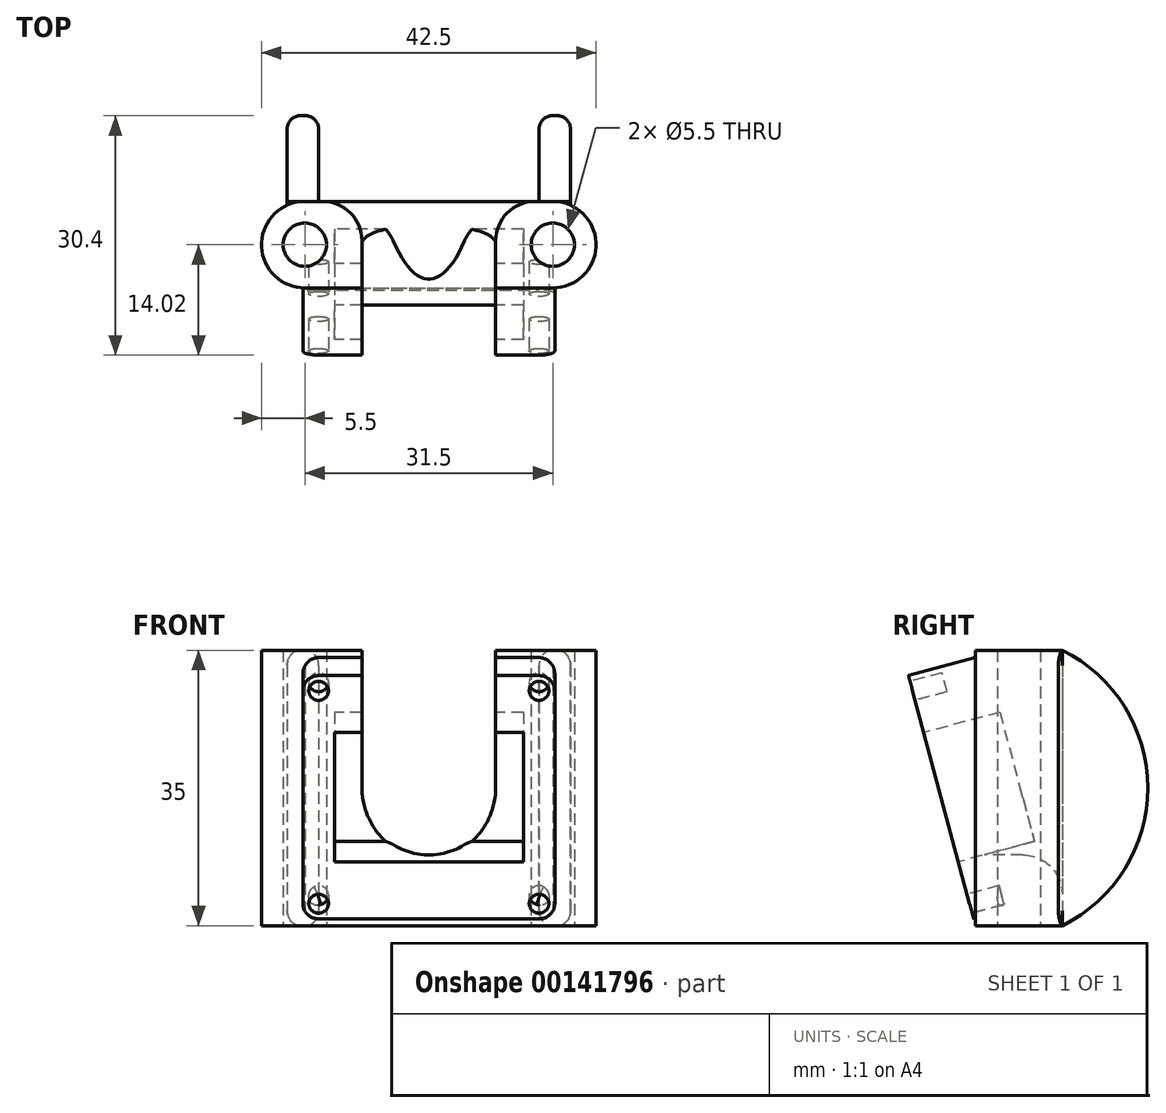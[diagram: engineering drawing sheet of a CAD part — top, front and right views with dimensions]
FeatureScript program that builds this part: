
annotation { "Feature Type Name" : "Feature", "Feature Type Description" : "" }
export const myFeature = defineFeature(function(context is Context, id is Id, definition is map)
    precondition{}
    {
        {
            var Q0;
            Q0=qCreatedBy(makeId("Top.planeOp"),FACE);
            var sketch = newSketch(context, id + "F0", { "sketchPlane" : qUnion([Q0])});
            skLineSegment(sketch, "E0", {"start": v(-18.5, 0) * mm, "end": v(18.5, 0) * mm, "construction": true});
            skCircle(sketch, "E1", {"center": v(-15.75, 0) * mm, "radius": 2.75 * mm});
            skCircle(sketch, "E2", {"center": v(15.75, 0) * mm, "radius": 2.75 * mm});
            skArc(sketch, "E3", {"start": v(-15.75, 5.5) * mm, "mid": v(-21.25, 0) * mm, "end": v(-15.75, -5.5) * mm});
            skArc(sketch, "E4", {"start": v(15.75, -5.5) * mm, "mid": v(21.25, 0) * mm, "end": v(15.75, 5.5) * mm});
            skLineSegment(sketch, "E5", {"start": v(-15.75, 5.5) * mm, "end": v(15.75, 5.5) * mm});
            skLineSegment(sketch, "E6", {"start": v(-15.75, -5.5) * mm, "end": v(15.75, -5.5) * mm});
            skSolve(sketch);
        }
        {
            var Q0;
            Q0=makeQuery(id+"F0.imprint","IMPRINT",FACE,{"disambiguationData":[TD([[makeQuery(id+"F0.imprint","IMPRINT",EDGE,{"derivedFrom":sQuery(id+"F0.wireOp",EDGE,"E1")}),-1.0]])]});
            extrude(context, id + "F1", {"entities" : qUnion([Q0]), "depth" : 35 * mm});
        }
        {
            var Q0;
            Q0=makeQuery(id+"F1.opExtrude","SWEPT_FACE",FACE,{"disambiguationData":[OSD([sQuery(id+"F0.wireOp",EDGE,"E6")])]});
            var sketch = newSketch(context, id + "F2", { "sketchPlane" : qUnion([Q0])});
            skLineSegment(sketch, "E7", {"start": v(-15.75, 35) * mm, "end": v(15.75, 0) * mm, "construction": true});
            skArc(sketch, "E8", {"start": v(-8.5, 17.5) * mm, "mid": v(0, 9) * mm, "end": v(8.5, 17.5) * mm});
            skLineSegment(sketch, "E9", {"start": v(-8.5, 17.5) * mm, "end": v(-8.5, 35) * mm});
            skLineSegment(sketch, "E10", {"start": v(8.5, 17.5) * mm, "end": v(8.5, 35) * mm});
            skLineSegment(sketch, "E11", {"start": v(8.5, 35) * mm, "end": v(-8.5, 35) * mm});
            skSolve(sketch);
        }
        {
            var Q0;
            Q0=qSketchRegion(id+"F2",true);
            extrude(context, id + "F3", {"entities" : qUnion([Q0]), "operationType" : NewBodyOperationType.REMOVE, "endBound" : BoundingType.THROUGH_ALL, "oppositeDirection" : true, "depth" : 25 * mm});
        }
        {
            var Q0;
            Q0=makeQuery(id+"F1.opExtrude","CAP_EDGE",EDGE,{"disambiguationData":[OSD([sQuery(id+"F0.wireOp",EDGE,"E6")])],"isStart":true});
            cPlane(context, id + "F4", {"entities" : qUnion([Q0]), "cplaneType" : CPlaneType.LINE_ANGLE, "offset" : 150 * mm, "angle" : 15 * degree, "width" : 150 * mm, "height" : 150 * mm});
        }
        {
            var Q0;
            Q0=qCreatedBy(id+"F4.planeOp",FACE);
            var sketch = newSketch(context, id + "F5", { "sketchPlane" : qUnion([Q0])});
            skPoint(sketch, "E12.0", {"position": v(15.75, 1.42) * mm});
            skPoint(sketch, "E13.0", {"position": v(-15.75, 35.23) * mm});
            skLineSegment(sketch, "E14", {"start": v(-15.75, 35.23) * mm, "end": v(15.75, 1.42) * mm, "construction": true});
            skLineSegment(sketch, "E15.rect.bottom", {"start": v(14, 32.33) * mm, "end": v(-14, 32.33) * mm, "construction": true});
            skLineSegment(sketch, "E15.rect.top", {"start": v(14, 4.33) * mm, "end": v(-14, 4.33) * mm, "construction": true});
            skLineSegment(sketch, "E15.rect.left", {"start": v(14, 32.33) * mm, "end": v(14, 4.33) * mm, "construction": true});
            skLineSegment(sketch, "E15.rect.right", {"start": v(-14, 32.33) * mm, "end": v(-14, 4.33) * mm, "construction": true});
            skPoint(sketch, "E15.rect.middle", {"position": v(0, 18.33) * mm});
            skLineSegment(sketch, "E16.0", {"start": v(14, 34.33) * mm, "end": v(-14, 34.33) * mm});
            skLineSegment(sketch, "E16.1", {"start": v(16, 32.33) * mm, "end": v(16, 4.33) * mm});
            skLineSegment(sketch, "E16.2", {"start": v(14, 2.33) * mm, "end": v(-14, 2.33) * mm});
            skLineSegment(sketch, "E16.3", {"start": v(-16, 32.33) * mm, "end": v(-16, 4.33) * mm});
            skPoint(sketch, "E17.visualSharp", {"position": v(16, 34.33) * mm});
            skArc(sketch, "E17.filletArc", {"start": v(16, 32.33) * mm, "mid": v(15.41, 33.74) * mm, "end": v(14, 34.33) * mm});
            skPoint(sketch, "E18.visualSharp", {"position": v(16, 2.33) * mm});
            skArc(sketch, "E18.filletArc", {"start": v(14, 2.33) * mm, "mid": v(15.41, 2.91) * mm, "end": v(16, 4.33) * mm});
            skPoint(sketch, "E19.visualSharp", {"position": v(-16, 2.33) * mm});
            skArc(sketch, "E19.filletArc", {"start": v(-16, 4.33) * mm, "mid": v(-15.41, 2.91) * mm, "end": v(-14, 2.33) * mm});
            skPoint(sketch, "E20.visualSharp", {"position": v(-16, 34.33) * mm});
            skArc(sketch, "E20.filletArc", {"start": v(-14, 34.33) * mm, "mid": v(-15.41, 33.74) * mm, "end": v(-16, 32.33) * mm});
            skSolve(sketch);
        }
        {
            var Q0;
            Q0=makeQuery(id+"F5.imprint","IMPRINT",FACE,{"disambiguationData":[TD([[makeQuery(id+"F5.imprint","IMPRINT",EDGE,{"derivedFrom":sQuery(id+"F5.wireOp",EDGE,"E16.0")}),1.0]])]});
            var Q1;
            Q1=makeQuery(id+"F1.opExtrude","SWEPT_FACE",FACE,{"disambiguationData":[OSD([sQuery(id+"F0.wireOp",EDGE,"E6")])]});
            extrude(context, id + "F6", {"entities" : qUnion([Q0]), "operationType" : NewBodyOperationType.ADD, "endBound" : BoundingType.UP_TO_SURFACE, "endBoundEntityFace" : qUnion([Q1]), "depth" : 25 * mm});
        }
        {
            var Q0;
            Q0=makeQuery(id+"F1.opExtrude","SWEPT_FACE",FACE,{"disambiguationData":[OSD([sQuery(id+"F0.wireOp",EDGE,"E5")])]});
            var sketch = newSketch(context, id + "F7", { "sketchPlane" : qUnion([Q0])});
            skLineSegment(sketch, "E21.0", {"start": v(-8.5, 35) * mm, "end": v(-8.5, 17.5) * mm});
            skLineSegment(sketch, "E22.0", {"start": v(8.5, 35) * mm, "end": v(8.5, 17.5) * mm});
            skArc(sketch, "E23.0", {"start": v(-8.5, 17.5) * mm, "mid": v(0, 9) * mm, "end": v(8.5, 17.5) * mm});
            skLineSegment(sketch, "E24", {"start": v(-8.5, 35) * mm, "end": v(8.5, 35) * mm});
            skSolve(sketch);
        }
        {
            var Q0;
            Q0=qSketchRegion(id+"F7",true);
            extrude(context, id + "F8", {"entities" : qUnion([Q0]), "operationType" : NewBodyOperationType.REMOVE, "oppositeDirection" : true, "depth" : 25 * mm});
        }
        {
            var Q0;
            Q0=makeQuery(id+"F6.opExtrude","CAP_FACE",FACE,{"disambiguationData":[OSD([sQuery(id+"F5.wireOp",EDGE,"E16.0"),sQuery(id+"F5.wireOp",EDGE,"E16.1"),sQuery(id+"F5.wireOp",EDGE,"E16.2"),sQuery(id+"F5.wireOp",EDGE,"E16.3"),sQuery(id+"F5.wireOp",EDGE,"E17.filletArc"),sQuery(id+"F5.wireOp",EDGE,"E18.filletArc"),sQuery(id+"F5.wireOp",EDGE,"E19.filletArc"),sQuery(id+"F5.wireOp",EDGE,"E20.filletArc")])],"isStart":true});
            var sketch = newSketch(context, id + "F9", { "sketchPlane" : qUnion([Q0])});
            skLineSegment(sketch, "E25", {"start": v(-16, 18.33) * mm, "end": v(16, 18.33) * mm, "construction": true});
            skLineSegment(sketch, "E26.rect.bottom", {"start": v(-14, 32.33) * mm, "end": v(14, 32.33) * mm, "construction": true});
            skLineSegment(sketch, "E26.rect.top", {"start": v(-14, 4.33) * mm, "end": v(14, 4.33) * mm, "construction": true});
            skLineSegment(sketch, "E26.rect.left", {"start": v(-14, 32.33) * mm, "end": v(-14, 4.33) * mm, "construction": true});
            skLineSegment(sketch, "E26.rect.right", {"start": v(14, 32.33) * mm, "end": v(14, 4.33) * mm, "construction": true});
            skPoint(sketch, "E26.rect.middle", {"position": v(0, 18.33) * mm});
            skCircle(sketch, "E27", {"center": v(-14, 32.33) * mm, "radius": 1.25 * mm});
            skCircle(sketch, "E28", {"center": v(14, 32.33) * mm, "radius": 1.25 * mm});
            skCircle(sketch, "E29", {"center": v(14, 4.33) * mm, "radius": 1.25 * mm});
            skCircle(sketch, "E30", {"center": v(-14, 4.33) * mm, "radius": 1.25 * mm});
            skSolve(sketch);
        }
        {
            var Q0;
            Q0=makeQuery(id+"F9.imprint","IMPRINT",FACE,{"disambiguationData":[TD([[makeQuery(id+"F9.imprint","IMPRINT",EDGE,{"derivedFrom":sQuery(id+"F9.wireOp",EDGE,"E27")}),1.0]])]});
            var Q1;
            Q1=makeQuery(id+"F9.imprint","IMPRINT",FACE,{"disambiguationData":[TD([[makeQuery(id+"F9.imprint","IMPRINT",EDGE,{"derivedFrom":sQuery(id+"F9.wireOp",EDGE,"E28")}),1.0]])]});
            var Q2;
            Q2=makeQuery(id+"F9.imprint","IMPRINT",FACE,{"disambiguationData":[TD([[makeQuery(id+"F9.imprint","IMPRINT",EDGE,{"derivedFrom":sQuery(id+"F9.wireOp",EDGE,"E29")}),1.0]])]});
            var Q3;
            Q3=makeQuery(id+"F9.imprint","IMPRINT",FACE,{"disambiguationData":[TD([[makeQuery(id+"F9.imprint","IMPRINT",EDGE,{"derivedFrom":sQuery(id+"F9.wireOp",EDGE,"E30")}),1.0]])]});
            extrude(context, id + "F10", {"entities" : qUnion([Q0, Q1, Q2, Q3]), "operationType" : NewBodyOperationType.REMOVE, "oppositeDirection" : true, "depth" : 4.2 * mm});
        }
        {
            var Q0;
            Q0=makeQuery(id+"F6.opExtrude","CAP_FACE",FACE,{"disambiguationData":[OSD([sQuery(id+"F5.wireOp",EDGE,"E16.0"),sQuery(id+"F5.wireOp",EDGE,"E16.1"),sQuery(id+"F5.wireOp",EDGE,"E16.2"),sQuery(id+"F5.wireOp",EDGE,"E16.3"),sQuery(id+"F5.wireOp",EDGE,"E17.filletArc"),sQuery(id+"F5.wireOp",EDGE,"E18.filletArc"),sQuery(id+"F5.wireOp",EDGE,"E19.filletArc"),sQuery(id+"F5.wireOp",EDGE,"E20.filletArc")])],"isStart":true});
            var sketch = newSketch(context, id + "F11", { "sketchPlane" : qUnion([Q0])});
            skLineSegment(sketch, "E31", {"start": v(-14, 32.33) * mm, "end": v(14, 4.33) * mm, "construction": true});
            skLineSegment(sketch, "E32.rect.bottom", {"start": v(12, 26.83) * mm, "end": v(-12, 26.83) * mm});
            skLineSegment(sketch, "E32.rect.top", {"start": v(12, 9.83) * mm, "end": v(-12, 9.83) * mm});
            skLineSegment(sketch, "E32.rect.left", {"start": v(12, 26.83) * mm, "end": v(12, 9.83) * mm});
            skLineSegment(sketch, "E32.rect.right", {"start": v(-12, 26.83) * mm, "end": v(-12, 9.83) * mm});
            skPoint(sketch, "E32.rect.middle", {"position": v(0, 18.33) * mm});
            skSolve(sketch);
        }
        {
            var Q0;
            {var subQ1=makeQuery(id+"F6.opExtrude","CAP_FACE",FACE,{"disambiguationData":[OSD([sQuery(id+"F5.wireOp",EDGE,"E16.0"),sQuery(id+"F5.wireOp",EDGE,"E16.1"),sQuery(id+"F5.wireOp",EDGE,"E16.2"),sQuery(id+"F5.wireOp",EDGE,"E16.3"),sQuery(id+"F5.wireOp",EDGE,"E17.filletArc"),sQuery(id+"F5.wireOp",EDGE,"E18.filletArc"),sQuery(id+"F5.wireOp",EDGE,"E19.filletArc"),sQuery(id+"F5.wireOp",EDGE,"E20.filletArc")])],"isStart":true});var subQ6=makeQuery(id+"F8.boolean.opBoolean","INTERSECT",EDGE,{"derivedFrom":[subQ1,makeQuery(id+"F8.opExtrude","SWEPT_FACE",FACE,{"disambiguationData":[OSD([sQuery(id+"F7.wireOp",EDGE,"E23.0")])]})]});Q0=makeQuery(id+"F11.imprint","IMPRINT",FACE,{"disambiguationData":[TD([[makeQuery(id+"F11.imprint","IMPRINT",EDGE,{"derivedFrom":subQ6}),-1.0]])]});}
            var Q1;
            Q1=makeQuery(id+"F11.imprint","IMPRINT",FACE,{"disambiguationData":[TD([[makeQuery(id+"F11.imprint","IMPRINT",EDGE,{"derivedFrom":sQuery(id+"F11.wireOp",EDGE,"E32.rect.top")}),-1.0]])]});
            extrude(context, id + "F12", {"entities" : qUnion([Q0, Q1]), "operationType" : NewBodyOperationType.REMOVE, "oppositeDirection" : true, "depth" : 10 * mm});
        }
        {
            var Q0;
            Q0=makeQuery(id+"F6.opExtrude","SWEPT_FACE",FACE,{"disambiguationData":[OSD([sQuery(id+"F5.wireOp",EDGE,"E16.3")])]});
            var sketch = newSketch(context, id + "F13", { "sketchPlane" : qUnion([Q0])});
            skPoint(sketch, "E33.0", {"position": v(5.5, 35) * mm});
            skPoint(sketch, "E34.0", {"position": v(5.5, 0) * mm});
            skLineSegment(sketch, "E35.0", {"start": v(5.5, 35) * mm, "end": v(5.5, 0) * mm});
            skArc(sketch, "E36", {"start": v(5.5, 0) * mm, "mid": v(16.38, 17.5) * mm, "end": v(5.5, 35) * mm});
            skSolve(sketch);
        }
        {
            var Q0;
            Q0=makeQuery(id+"F13.imprint","IMPRINT",FACE,{"disambiguationData":[TD([[makeQuery(id+"F13.imprint","IMPRINT",EDGE,{"derivedFrom":sQuery(id+"F13.wireOp",EDGE,"E35.0")}),1.0]])]});
            extrude(context, id + "F14", {"entities" : qUnion([Q0]), "operationType" : NewBodyOperationType.ADD, "depth" : 2 * mm, "hasSecondDirection" : true, "secondDirectionOppositeDirection" : true, "secondDirectionDepth" : 2 * mm});
        }
        {
            var Q0;
            Q0=makeQuery(id+"F1.opExtrude","SWEPT_BODY",BODY,{"disambiguationData":[OSD([sQuery(id+"F0.wireOp",EDGE,"E1"),sQuery(id+"F0.wireOp",EDGE,"E2"),sQuery(id+"F0.wireOp",EDGE,"E3"),sQuery(id+"F0.wireOp",EDGE,"E4"),sQuery(id+"F0.wireOp",EDGE,"E5"),sQuery(id+"F0.wireOp",EDGE,"E6")])]});
            var Q1;
            Q1=qCreatedBy(makeId("Right.planeOp"),FACE);
            mirror(context, id + "F15", {"operationType" : NewBodyOperationType.ADD, "entities" : qUnion([Q0]), "mirrorPlane" : qUnion([Q1])});
        }
        {
            var Q0;
            Q0=makeQuery(id+"F14.opExtrude","CAP_EDGE",EDGE,{"disambiguationData":[OSD([sQuery(id+"F13.wireOp",EDGE,"E36")])],"isStart":false});
            var Q1;
            Q1=makeQuery(id+"F14.opExtrude","CAP_EDGE",EDGE,{"disambiguationData":[OSD([sQuery(id+"F13.wireOp",EDGE,"E36")])],"isStart":true});
            var Q2;
            Q2=makeQuery(id+"F15.opPattern","COPY",EDGE,{"derivedFrom":makeQuery(id+"F14.opExtrude","CAP_EDGE",EDGE,{"disambiguationData":[OSD([sQuery(id+"F13.wireOp",EDGE,"E36")])],"isStart":true}),"instanceName":"1"});
            var Q3;
            Q3=makeQuery(id+"F15.opPattern","COPY",EDGE,{"derivedFrom":makeQuery(id+"F14.opExtrude","CAP_EDGE",EDGE,{"disambiguationData":[OSD([sQuery(id+"F13.wireOp",EDGE,"E36")])],"isStart":false}),"instanceName":"1"});
            fillet(context, id + "F16", {"entities" : qUnion([Q0, Q1, Q2, Q3]), "radius" : 1.7 * mm, "tangentPropagation" : true, "allowEdgeOverflow" : false});
        }
        {
            var Q0;
            Q0=makeQuery(id+"F3.boolean.opBoolean","INTERSECT",EDGE,{"derivedFrom":[makeQuery(id+"F1.opExtrude","SWEPT_FACE",FACE,{"disambiguationData":[OSD([sQuery(id+"F0.wireOp",EDGE,"E5")])]}),makeQuery(id+"F3.opExtrude","SWEPT_FACE",FACE,{"disambiguationData":[OSD([sQuery(id+"F2.wireOp",EDGE,"E10")])]})]});
            fillet(context, id + "F17", {"entities" : qUnion([Q0]), "radius" : 5 * mm, "tangentPropagation" : true, "allowEdgeOverflow" : false});
        }
        {
            var Q0;
            Q0=makeQuery(id+"F14.opExtrude","SWEPT_FACE",FACE,{"disambiguationData":[OSD([sQuery(id+"F13.wireOp",EDGE,"E35.0")])]});
            var Q1;
            Q1=makeQuery(id+"F1.opExtrude","SWEPT_FACE",FACE,{"disambiguationData":[OSD([sQuery(id+"F0.wireOp",EDGE,"E4")])]});
            extrude(context, id + "F18", {"entities" : qUnion([Q0]), "operationType" : NewBodyOperationType.ADD, "endBound" : BoundingType.UP_TO_SURFACE, "endBoundEntityFace" : qUnion([Q1]), "depth" : 25 * mm});
        }
        {
            var Q0;
            Q0=makeQuery(id+"F15.opPattern","COPY",FACE,{"derivedFrom":makeQuery(id+"F14.opExtrude","SWEPT_FACE",FACE,{"disambiguationData":[OSD([sQuery(id+"F13.wireOp",EDGE,"E35.0")])]}),"instanceName":"1"});
            var Q1;
            Q1=makeQuery(id+"F1.opExtrude","SWEPT_FACE",FACE,{"disambiguationData":[OSD([sQuery(id+"F0.wireOp",EDGE,"E3")])]});
            extrude(context, id + "F19", {"entities" : qUnion([Q0]), "operationType" : NewBodyOperationType.ADD, "endBound" : BoundingType.UP_TO_SURFACE, "endBoundEntityFace" : qUnion([Q1]), "depth" : 25 * mm});
        }
    });
